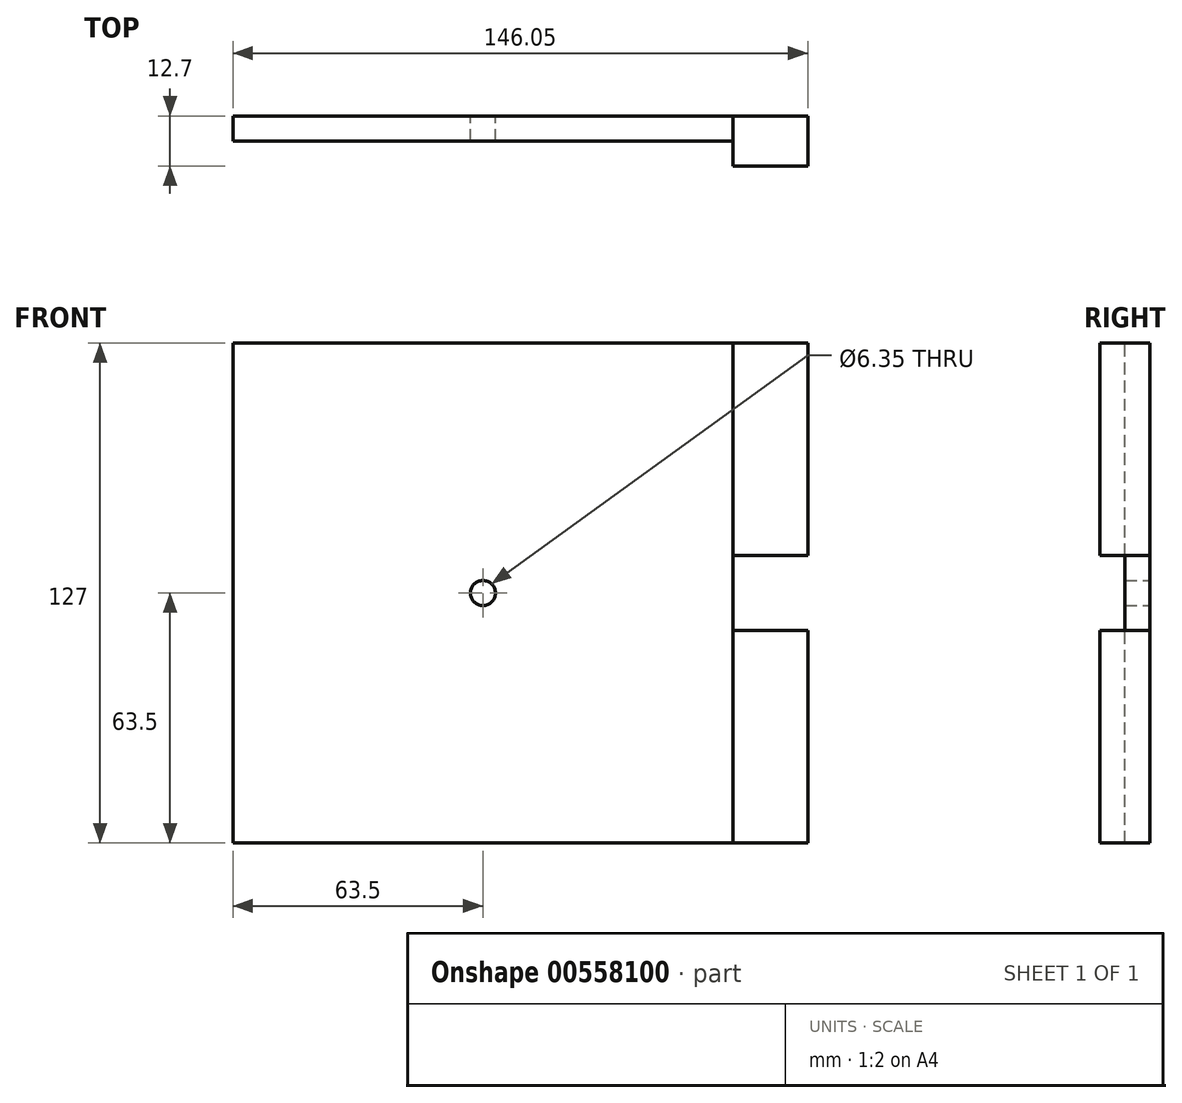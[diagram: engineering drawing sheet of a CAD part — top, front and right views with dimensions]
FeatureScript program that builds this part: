
annotation { "Feature Type Name" : "Feature", "Feature Type Description" : "" }
export const myFeature = defineFeature(function(context is Context, id is Id, definition is map)
    precondition{}
    {
        {
            var Q0;
            Q0=qCreatedBy(makeId("Front.planeOp"),FACE);
            var sketch = newSketch(context, id + "F0", { "sketchPlane" : qUnion([Q0])});
            skLineSegment(sketch, "E0.bottom", {"start": v(63.5, -63.5) * mm, "end": v(-63.5, -63.5) * mm});
            skLineSegment(sketch, "E0.top", {"start": v(63.5, 63.5) * mm, "end": v(-63.5, 63.5) * mm});
            skLineSegment(sketch, "E0.left", {"start": v(63.5, -63.5) * mm, "end": v(63.5, 63.5) * mm});
            skLineSegment(sketch, "E0.right", {"start": v(-63.5, -63.5) * mm, "end": v(-63.5, 63.5) * mm});
            skPoint(sketch, "E0.middle", {"position": v(0, 0) * mm});
            skCircle(sketch, "E1", {"center": v(0, 0) * mm, "radius": 3.18 * mm});
            skSolve(sketch);
        }
        {
            var Q0;
            Q0=qCreatedBy(makeId("Front.planeOp"),FACE);
            var sketch = newSketch(context, id + "F1", { "sketchPlane" : qUnion([Q0])});
            skLineSegment(sketch, "E2.left", {"start": v(63.5, -63.5) * mm, "end": v(63.5, -9.52) * mm});
            skPoint(sketch, "E2.middle", {"position": v(0, 0) * mm});
            skLineSegment(sketch, "E3.bottom", {"start": v(63.5, 63.5) * mm, "end": v(82.55, 63.5) * mm});
            skLineSegment(sketch, "E3.top", {"start": v(63.5, 9.53) * mm, "end": v(82.55, 9.53) * mm});
            skLineSegment(sketch, "E3.left", {"start": v(63.5, 63.5) * mm, "end": v(63.5, 9.53) * mm});
            skLineSegment(sketch, "E3.right", {"start": v(82.55, 63.5) * mm, "end": v(82.55, 9.53) * mm});
            skLineSegment(sketch, "E4.bottom", {"start": v(63.5, -63.5) * mm, "end": v(82.55, -63.5) * mm});
            skLineSegment(sketch, "E4.top", {"start": v(63.5, -9.52) * mm, "end": v(82.55, -9.52) * mm});
            skLineSegment(sketch, "E4.right", {"start": v(82.55, -63.5) * mm, "end": v(82.55, -9.52) * mm});
            skPoint(sketch, "E2.top.end.orphan", {"position": v(-63.5, 63.5) * mm});
            skPoint(sketch, "E2.bottom.end.orphan", {"position": v(-63.5, -63.5) * mm});
            skLineSegment(sketch, "E5.trimOffspring", {"start": v(63.5, 9.53) * mm, "end": v(63.5, 63.5) * mm});
            skSolve(sketch);
        }
        {
            var Q0;
            Q0 = qSketchRegion(id + "F1", true);
            extrude(context, id + "F2", {"entities" : qUnion([Q0]), "depth" : 12.7 * mm, "offsetDistance" : 25.4 * mm});
        }
        {
            var Q0;
            Q0 = qSketchRegion(id + "F0", true);
            extrude(context, id + "F3", {"entities" : qUnion([Q0]), "depth" : 6.35 * mm, "offsetDistance" : 25.4 * mm});
        }
    });
